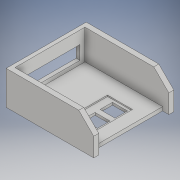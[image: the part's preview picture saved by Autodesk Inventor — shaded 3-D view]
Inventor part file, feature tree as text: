
AUTODESK INVENTOR PART (.ipt)
format: ipt  version: 2018 (Build 220112000, 112)  size: 182,784 bytes
history: native  units: in
note: dims shown in document units (in); Inventor stores cm internally (conversion verified against a paired STEP export)
features: extrude x6, sketch x6, chamfer x1
ambient origin geometry x8: Origin, YZ Plane, XZ Plane, XY Plane, X Axis, Y Axis, Z Axis, Center Point
bodies: Solid1 (feature_tree)
feature tree (13):
  extrude  "Extrusion1"  Depth=6.2992in
  extrude  "Extrusion2"  TaperAngle=0.0deg  [1 undecoded]
  extrude  "Extrusion3"  Depth=0.3937in
  extrude  "Extrusion4"  Depth=6.5945in
  chamfer  "Chamfer1"  Distance=2.3622in
  extrude  "Extrusion5"  Depth=0.7874in
  extrude  "Extrusion6"  Depth=0.2953in
  sketch  "Sketch1"  dims[d0=6.8898in d1=6.2992in]
  sketch  "Sketch2"  dims[d2=0.2953in d3=0.0in]
  sketch  "Sketch3"  dims[d4=0.3937in d5=0.3937in]
  sketch  "Sketch4"  dims[d6=5.5118in d7=6.5945in]
  sketch  "Sketch5"  dims[d8=0.4921in d9=2.3622in d10=0.0in]
  sketch  "Sketch6"  dims[d11=0.7874in d12=0.7874in d13=0.2953in d14=0.9843in d15=4.7244in d16=1.0827in d17=2.3622in d18=0.0in d19=0.2953in d20=0.0in d21=0.4921in d22=0.2953in d23=0.0in d24=1.1811in d25=0.0492in d26=45.0deg d27=1.1811in d28=1.1811in d29=0.3937in d30=1.9685in d31=1.9685in d32=0.9843in d33=1.1811in d34=1.1811in d35=0.2953in d36=0.0in d37=0.1969in d38=0.5906in d39=0.1969in d40=0.1969in d41=0.0984in d42=0.0in]
note: 1 required parameter value undecoded (feature->parameter linkage not recoverable at this tier; creation-order binding heuristic only, values carry confidence <= 0.55)
